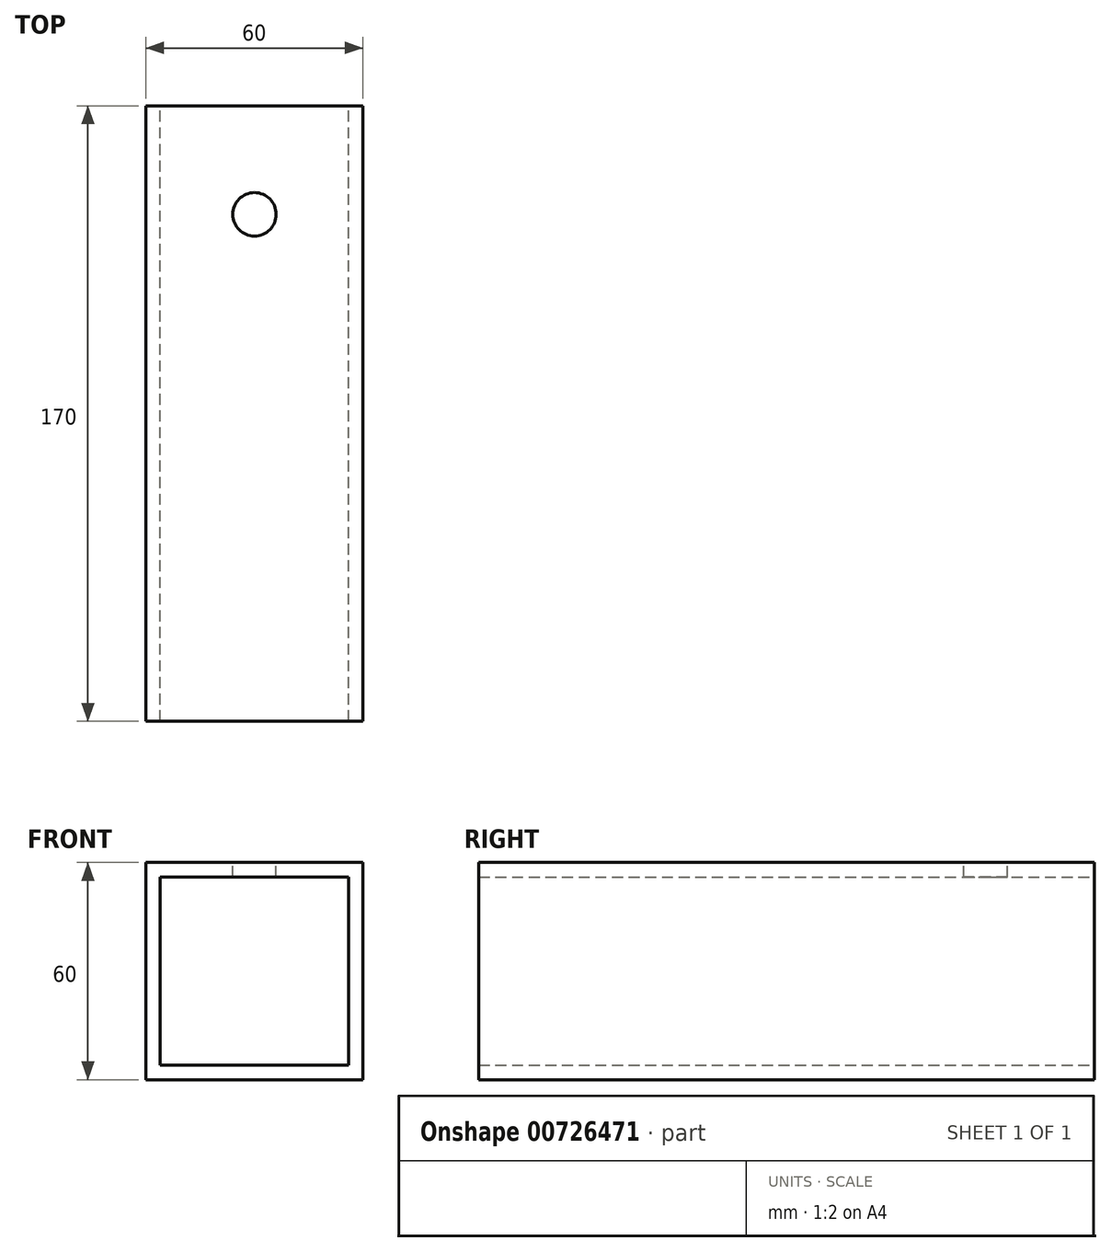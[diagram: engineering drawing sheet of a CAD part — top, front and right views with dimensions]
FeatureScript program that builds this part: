
annotation { "Feature Type Name" : "Feature", "Feature Type Description" : "" }
export const myFeature = defineFeature(function(context is Context, id is Id, definition is map)
    precondition{}
    {
        {
            var Q0;
            Q0=qCreatedBy(makeId("Front.planeOp"),FACE);
            var sketch = newSketch(context, id + "F0", { "sketchPlane" : qUnion([Q0])});
            skLineSegment(sketch, "E0.bottom", {"start": v(0, 0) * mm, "end": v(60, 0) * mm});
            skLineSegment(sketch, "E0.top", {"start": v(0, 60) * mm, "end": v(60, 60) * mm});
            skLineSegment(sketch, "E0.left", {"start": v(0, 0) * mm, "end": v(0, 60) * mm});
            skLineSegment(sketch, "E0.right", {"start": v(60, 0) * mm, "end": v(60, 60) * mm});
            skLineSegment(sketch, "E1.bottom", {"start": v(4, 4) * mm, "end": v(56, 4) * mm});
            skLineSegment(sketch, "E1.top", {"start": v(4, 56) * mm, "end": v(56, 56) * mm});
            skLineSegment(sketch, "E1.left", {"start": v(4, 4) * mm, "end": v(4, 56) * mm});
            skLineSegment(sketch, "E1.right", {"start": v(56, 4) * mm, "end": v(56, 56) * mm});
            skSolve(sketch);
        }
        {
            var Q0;
            Q0=makeQuery(id+"F0.imprint","IMPRINT",FACE,{"disambiguationData":[TD([[makeQuery(id+"F0.imprint","IMPRINT",EDGE,{"derivedFrom":sQuery(id+"F0.wireOp",EDGE,"E0.bottom")}),1.0]])]});
            extrude(context, id + "F1", {"entities" : qUnion([Q0]), "depth" : 170 * mm, "offsetDistance" : 25 * mm});
        }
        {
            var Q0;
            Q0=makeQuery(id+"F1.opExtrude","SWEPT_FACE",FACE,{"disambiguationData":[OSD([sQuery(id+"F0.wireOp",EDGE,"E0.top")])]});
            var sketch = newSketch(context, id + "F2", { "sketchPlane" : qUnion([Q0])});
            skCircle(sketch, "E2", {"center": v(30, -30) * mm, "radius": 6 * mm});
            skSolve(sketch);
        }
        {
            var Q0;
            Q0=makeQuery(id+"F2.imprint","IMPRINT",FACE,{"disambiguationData":[TD([[makeQuery(id+"F2.imprint","IMPRINT",EDGE,{"derivedFrom":sQuery(id+"F2.wireOp",EDGE,"E2")}),1.0]])]});
            extrude(context, id + "F3", {"entities" : qUnion([Q0]), "operationType" : NewBodyOperationType.REMOVE, "oppositeDirection" : true, "depth" : 10 * mm, "offsetDistance" : 25 * mm});
        }
    });
